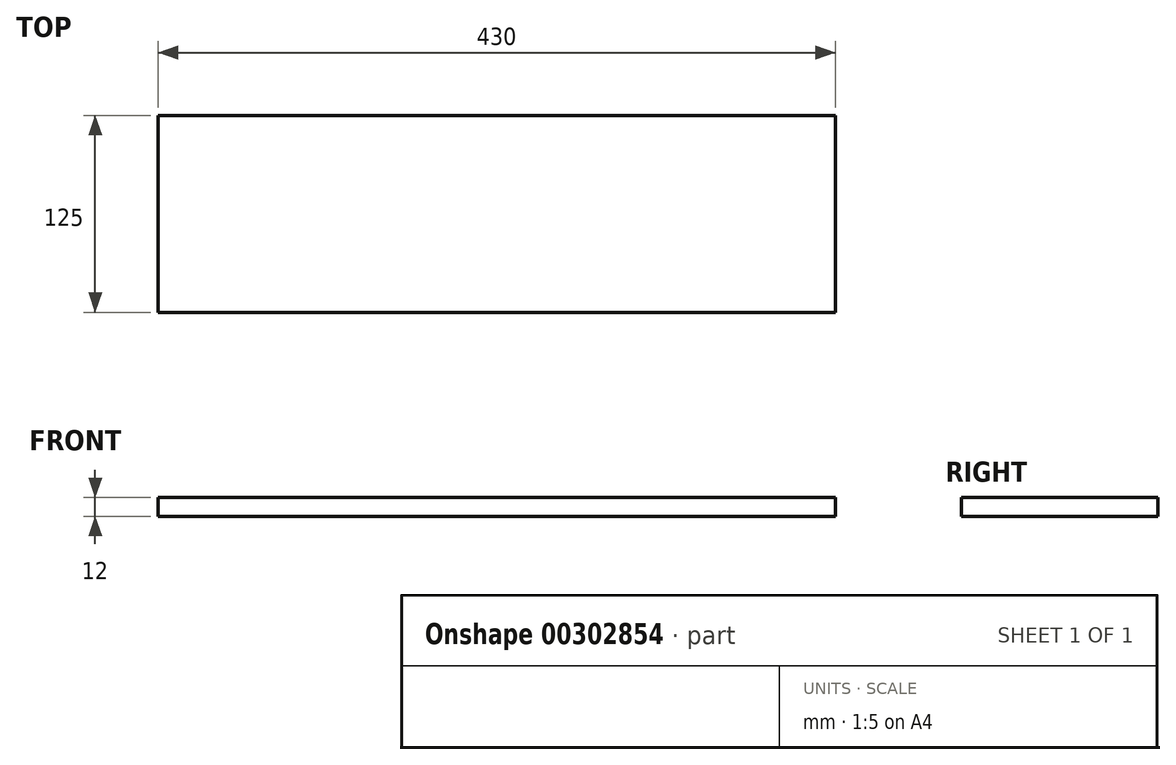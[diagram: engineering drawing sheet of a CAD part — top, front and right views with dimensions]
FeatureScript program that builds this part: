
annotation { "Feature Type Name" : "Feature", "Feature Type Description" : "" }
export const myFeature = defineFeature(function(context is Context, id is Id, definition is map)
    precondition{}
    {
        {
            var Q0;
            Q0=qCreatedBy(makeId("Top.planeOp"),FACE);
            var sketch = newSketch(context, id + "F0", { "sketchPlane" : qUnion([Q0])});
            skLineSegment(sketch, "E0.bottom", {"start": v(0, 0) * mm, "end": v(430, 0) * mm});
            skLineSegment(sketch, "E0.top", {"start": v(0, 125) * mm, "end": v(430, 125) * mm});
            skLineSegment(sketch, "E0.left", {"start": v(0, 0) * mm, "end": v(0, 125) * mm});
            skLineSegment(sketch, "E0.right", {"start": v(430, 0) * mm, "end": v(430, 125) * mm});
            skSolve(sketch);
        }
        {
            var Q0;
            Q0=qSketchRegion(id+"F0",true);
            extrude(context, id + "F1", {"entities" : qUnion([Q0]), "depth" : 12 * mm});
        }
    });
